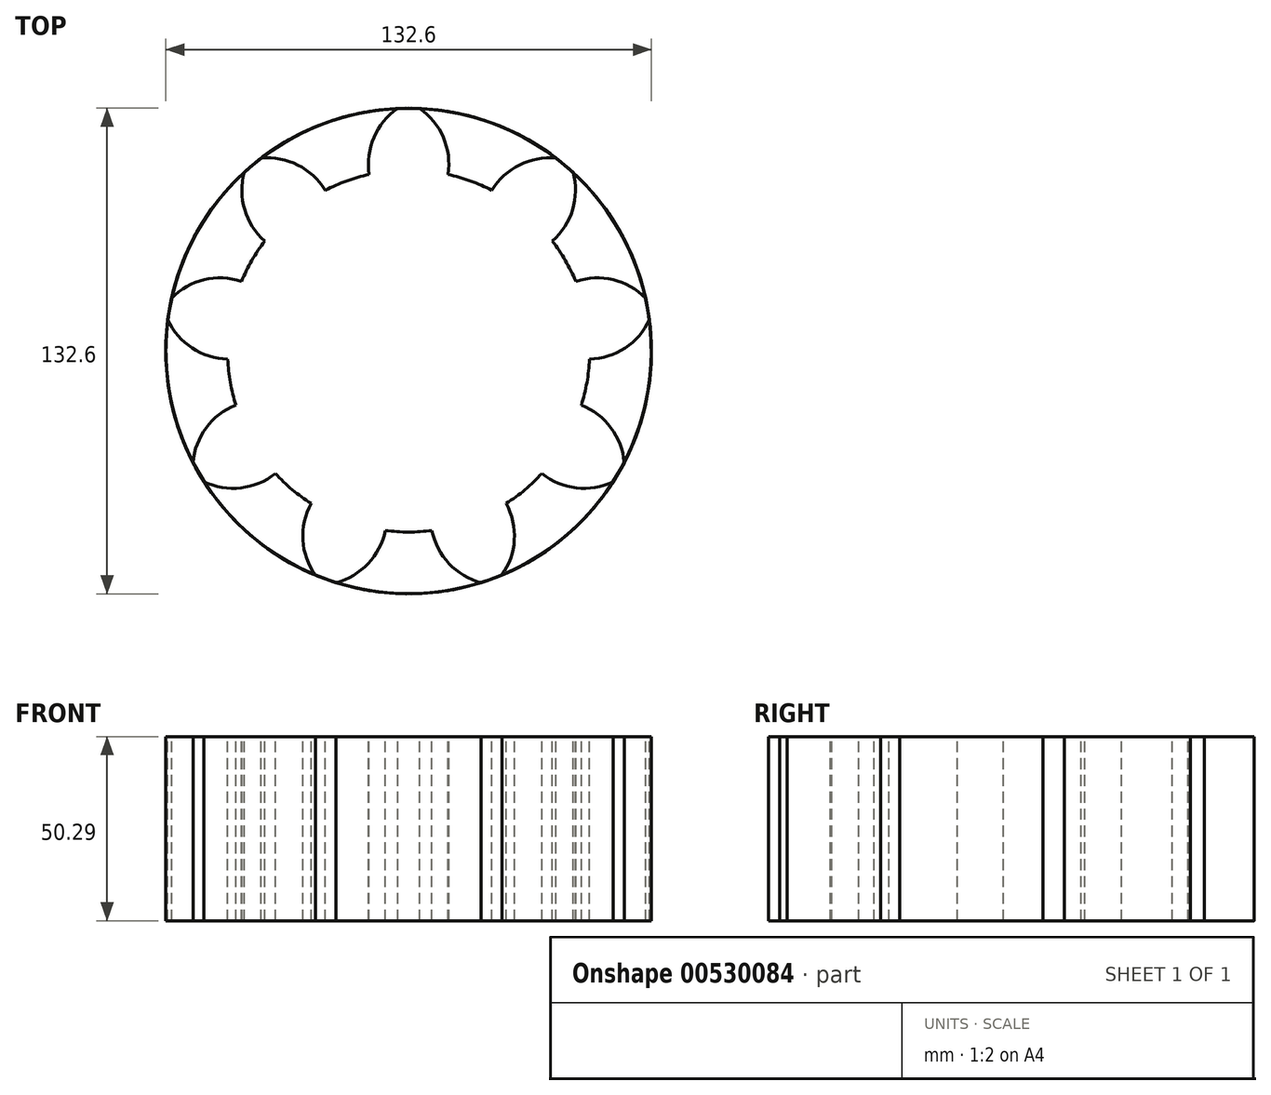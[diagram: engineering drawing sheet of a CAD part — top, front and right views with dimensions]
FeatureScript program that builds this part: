
annotation { "Feature Type Name" : "Feature", "Feature Type Description" : "" }
export const myFeature = defineFeature(function(context is Context, id is Id, definition is map)
    precondition{}
    {
        {
            var Q0;
            Q0=qCreatedBy(makeId("Top.planeOp"),FACE);
            var sketch = newSketch(context, id + "F0", { "sketchPlane" : qUnion([Q0])});
            skCircle(sketch, "E0", {"center": v(0, 0) * mm, "radius": 66.3 * mm});
            skSolve(sketch);
        }
        {
            var Q0;
            Q0 = qSketchRegion(id + "F0", true);
            extrude(context, id + "F1", {"entities" : qUnion([Q0]), "depth" : 50.3 * mm, "offsetDistance" : 25.4 * mm});
        }
        {
            var Q0;
            Q0=makeQuery(id+"F1.opExtrude","CAP_FACE",FACE,{"disambiguationData":[OSD([sQuery(id+"F0.wireOp",EDGE,"E0")])],"isStart":false});
            var sketch = newSketch(context, id + "F2", { "sketchPlane" : qUnion([Q0])});
            skArc(sketch, "E1", {"start": v(-6.37, -49.02) * mm, "mid": v(0, -49.44) * mm, "end": v(6.37, -49.02) * mm});
            skArc(sketch, "E2", {"start": v(-19.83, -63.26) * mm, "mid": v(-11.05, -58.08) * mm, "end": v(-6.37, -49.02) * mm});
            skArc(sketch, "E3.MirrorCS", {"start": v(19.83, -63.26) * mm, "mid": v(11.05, -58.08) * mm, "end": v(6.37, -49.02) * mm});
            skArc(sketch, "E4", {"start": v(-19.83, -63.26) * mm, "mid": v(0, -66.3) * mm, "end": v(19.83, -63.26) * mm});
            skSolve(sketch);
        }
        {
            var Q0;
            Q0 = qSketchRegion(id + "F2", true);
            extrude(context, id + "F3", {"entities" : qUnion([Q0]), "operationType" : NewBodyOperationType.REMOVE, "endBound" : BoundingType.THROUGH_ALL, "oppositeDirection" : true, "depth" : 25.4 * mm, "offsetDistance" : 25.4 * mm});
        }
        {
            var Q0;
            Q0=makeQuery(id+"F1.opExtrude","SWEPT_BODY",BODY,{"disambiguationData":[OSD([sQuery(id+"F0.wireOp",EDGE,"E0")])]});
            var Q1;
            Q1=makeQuery(id+"F1.opExtrude","SWEPT_FACE",FACE,{"disambiguationData":[OSD([sQuery(id+"F0.wireOp",EDGE,"E0")])]});
            circularPattern(context, id + "F4", {"entities" : qUnion([Q0]), "axis" : qUnion([Q1]), "angle" : 360 * degree, "instanceCount" : 9, "equalSpace" : true});
        }
    });
